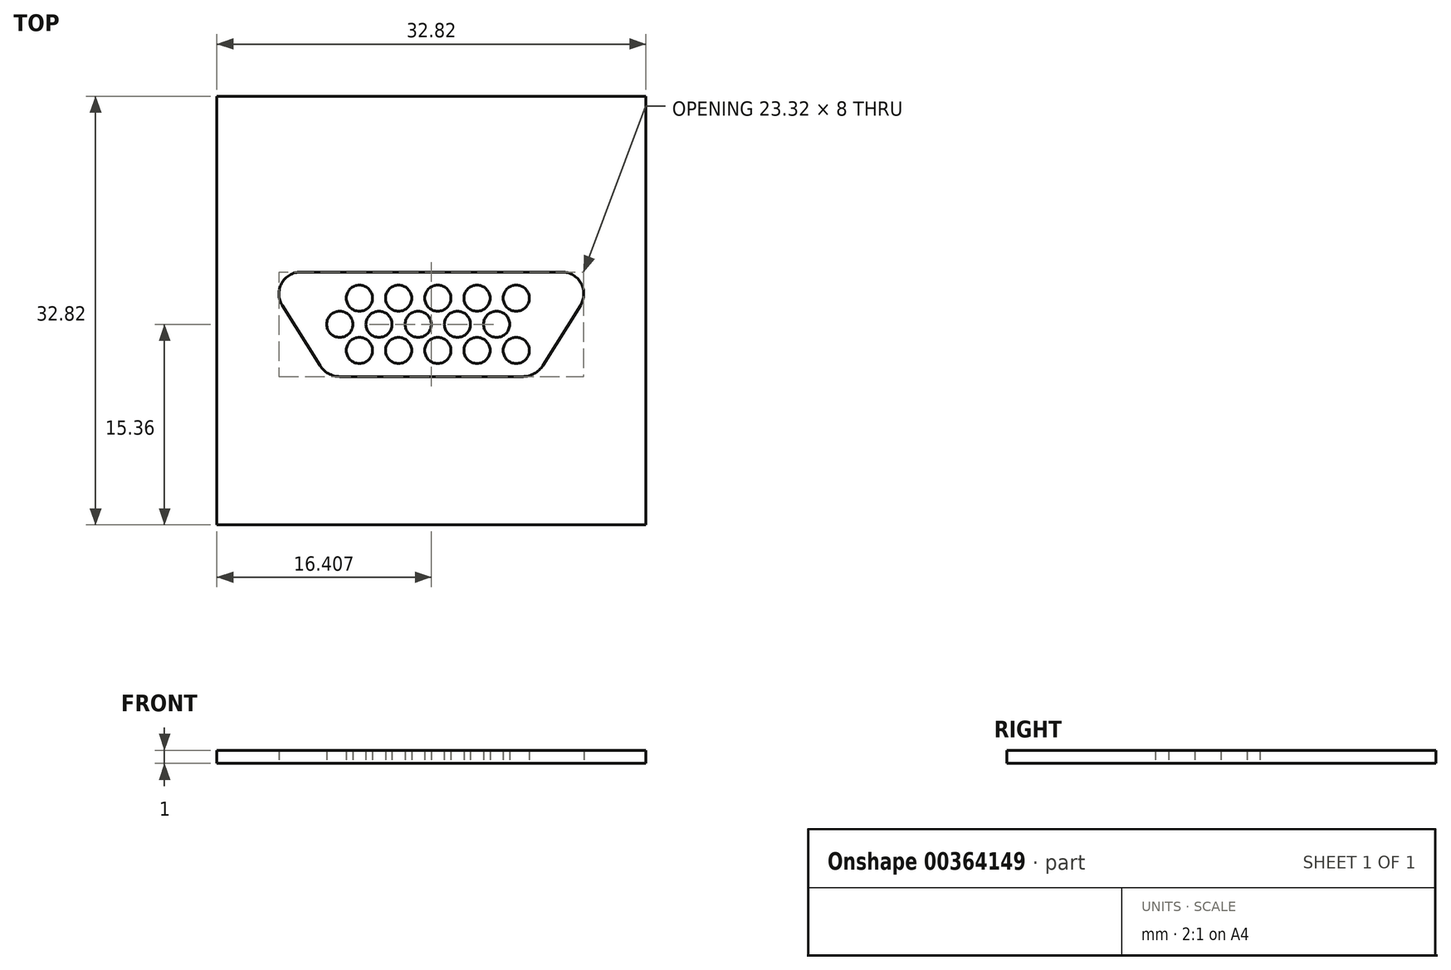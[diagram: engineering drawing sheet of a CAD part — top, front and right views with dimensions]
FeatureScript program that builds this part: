
annotation { "Feature Type Name" : "Feature", "Feature Type Description" : "" }
export const myFeature = defineFeature(function(context is Context, id is Id, definition is map)
    precondition{}
    {
        {
            var Q0;
            Q0=qCreatedBy(makeId("Top.planeOp"),FACE);
            var sketch = newSketch(context, id + "F0", { "sketchPlane" : qUnion([Q0])});
            skCircle(sketch, "E0", {"center": v(0, 0) * mm, "radius": 1 * mm});
            skCircle(sketch, "E1.1.0.0", {"center": v(3, 0) * mm, "radius": 1 * mm});
            skCircle(sketch, "E1.2.0.0", {"center": v(6, 0) * mm, "radius": 1 * mm});
            skLineSegment(sketch, "E1.direction1", {"start": v(0, 0) * mm, "end": v(3, 0) * mm, "construction": true});
            skCircle(sketch, "E2.1.0.0", {"center": v(-3, 0) * mm, "radius": 1 * mm});
            skCircle(sketch, "E2.2.0.0", {"center": v(-6, 0) * mm, "radius": 1 * mm});
            skLineSegment(sketch, "E2.direction1", {"start": v(0, 0) * mm, "end": v(-3, 0) * mm, "construction": true});
            skCircle(sketch, "E3", {"center": v(-4.5, 2) * mm, "radius": 1 * mm});
            skCircle(sketch, "E4.1.0.0", {"center": v(-1.5, 2) * mm, "radius": 1 * mm});
            skCircle(sketch, "E4.2.0.0", {"center": v(1.5, 2) * mm, "radius": 1 * mm});
            skCircle(sketch, "E4.3.0.0", {"center": v(4.5, 2) * mm, "radius": 1 * mm});
            skCircle(sketch, "E4.4.0.0", {"center": v(7.5, 2) * mm, "radius": 1 * mm});
            skLineSegment(sketch, "E4.direction1", {"start": v(-4.5, 2) * mm, "end": v(-1.5, 2) * mm, "construction": true});
            skCircle(sketch, "E5", {"center": v(-4.5, -2) * mm, "radius": 1 * mm});
            skCircle(sketch, "E6.1.0.0", {"center": v(-1.5, -2) * mm, "radius": 1 * mm});
            skCircle(sketch, "E6.2.0.0", {"center": v(1.5, -2) * mm, "radius": 1 * mm});
            skCircle(sketch, "E6.3.0.0", {"center": v(4.5, -2) * mm, "radius": 1 * mm});
            skCircle(sketch, "E6.4.0.0", {"center": v(7.5, -2) * mm, "radius": 1 * mm});
            skLineSegment(sketch, "E6.direction1", {"start": v(-4.5, -2) * mm, "end": v(-1.5, -2) * mm, "construction": true});
            skLineSegment(sketch, "E7", {"start": v(0, 4) * mm, "end": v(-9, 4) * mm});
            skLineSegment(sketch, "E8.MirrorCS", {"start": v(0, 4) * mm, "end": v(11, 4) * mm});
            skLineSegment(sketch, "E9", {"start": v(-10.4, 1.46) * mm, "end": v(-7.52, -3.15) * mm});
            skLineSegment(sketch, "E10", {"start": v(12.42, 1.46) * mm, "end": v(9.54, -3.15) * mm});
            skArc(sketch, "E11", {"start": v(-9, 4) * mm, "mid": v(-10.45, 3.14) * mm, "end": v(-10.4, 1.46) * mm});
            skArc(sketch, "E12", {"start": v(12.42, 1.46) * mm, "mid": v(12.46, 3.14) * mm, "end": v(11, 4) * mm});
            skLineSegment(sketch, "E13", {"start": v(-6, -4) * mm, "end": v(8, -4) * mm});
            skArc(sketch, "E14", {"start": v(-7.52, -3.15) * mm, "mid": v(-6.87, -3.77) * mm, "end": v(-6, -4) * mm});
            skArc(sketch, "E15", {"start": v(8, -4) * mm, "mid": v(8.88, -3.77) * mm, "end": v(9.54, -3.15) * mm});
            skLineSegment(sketch, "E16", {"start": v(17.42, 1.46) * mm, "end": v(17.42, 17.46) * mm});
            skLineSegment(sketch, "E17", {"start": v(17.42, 17.46) * mm, "end": v(-15.4, 17.46) * mm});
            skLineSegment(sketch, "E18.bottom", {"start": v(-15.4, 17.46) * mm, "end": v(17.42, 17.46) * mm});
            skLineSegment(sketch, "E18.top", {"start": v(-15.4, -15.36) * mm, "end": v(17.42, -15.36) * mm});
            skLineSegment(sketch, "E18.left", {"start": v(-15.4, 17.46) * mm, "end": v(-15.4, -15.36) * mm});
            skLineSegment(sketch, "E18.right", {"start": v(17.42, 17.46) * mm, "end": v(17.42, -15.36) * mm});
            skSolve(sketch);
        }
        {
            var Q0;
            Q0=makeQuery(id+"F0.imprint","IMPRINT",FACE,{"disambiguationData":[TD([[makeQuery(id+"F0.imprint","IMPRINT",EDGE,{"derivedFrom":sQuery(id+"F0.wireOp",EDGE,"E3")}),1.0]])]});
            var Q1;
            Q1=makeQuery(id+"F0.imprint","IMPRINT",FACE,{"disambiguationData":[TD([[makeQuery(id+"F0.imprint","IMPRINT",EDGE,{"derivedFrom":sQuery(id+"F0.wireOp",EDGE,"E4.1.0.0")}),1.0]])]});
            var Q2;
            Q2=makeQuery(id+"F0.imprint","IMPRINT",FACE,{"disambiguationData":[TD([[makeQuery(id+"F0.imprint","IMPRINT",EDGE,{"derivedFrom":sQuery(id+"F0.wireOp",EDGE,"E4.2.0.0")}),1.0]])]});
            var Q3;
            Q3=makeQuery(id+"F0.imprint","IMPRINT",FACE,{"disambiguationData":[TD([[makeQuery(id+"F0.imprint","IMPRINT",EDGE,{"derivedFrom":sQuery(id+"F0.wireOp",EDGE,"E4.3.0.0")}),1.0]])]});
            var Q4;
            Q4=makeQuery(id+"F0.imprint","IMPRINT",FACE,{"disambiguationData":[TD([[makeQuery(id+"F0.imprint","IMPRINT",EDGE,{"derivedFrom":sQuery(id+"F0.wireOp",EDGE,"E4.4.0.0")}),1.0]])]});
            var Q5;
            Q5=makeQuery(id+"F0.imprint","IMPRINT",FACE,{"disambiguationData":[TD([[makeQuery(id+"F0.imprint","IMPRINT",EDGE,{"derivedFrom":sQuery(id+"F0.wireOp",EDGE,"E1.2.0.0")}),1.0]])]});
            var Q6;
            Q6=makeQuery(id+"F0.imprint","IMPRINT",FACE,{"disambiguationData":[TD([[makeQuery(id+"F0.imprint","IMPRINT",EDGE,{"derivedFrom":sQuery(id+"F0.wireOp",EDGE,"E1.1.0.0")}),1.0]])]});
            var Q7;
            Q7=makeQuery(id+"F0.imprint","IMPRINT",FACE,{"disambiguationData":[TD([[makeQuery(id+"F0.imprint","IMPRINT",EDGE,{"derivedFrom":sQuery(id+"F0.wireOp",EDGE,"E0")}),1.0]])]});
            var Q8;
            Q8=makeQuery(id+"F0.imprint","IMPRINT",FACE,{"disambiguationData":[TD([[makeQuery(id+"F0.imprint","IMPRINT",EDGE,{"derivedFrom":sQuery(id+"F0.wireOp",EDGE,"E2.1.0.0")}),1.0]])]});
            var Q9;
            Q9=makeQuery(id+"F0.imprint","IMPRINT",FACE,{"disambiguationData":[TD([[makeQuery(id+"F0.imprint","IMPRINT",EDGE,{"derivedFrom":sQuery(id+"F0.wireOp",EDGE,"E2.2.0.0")}),1.0]])]});
            var Q10;
            Q10=makeQuery(id+"F0.imprint","IMPRINT",FACE,{"disambiguationData":[TD([[makeQuery(id+"F0.imprint","IMPRINT",EDGE,{"derivedFrom":sQuery(id+"F0.wireOp",EDGE,"E5")}),1.0]])]});
            var Q11;
            Q11=makeQuery(id+"F0.imprint","IMPRINT",FACE,{"disambiguationData":[TD([[makeQuery(id+"F0.imprint","IMPRINT",EDGE,{"derivedFrom":sQuery(id+"F0.wireOp",EDGE,"E6.1.0.0")}),1.0]])]});
            var Q12;
            Q12=makeQuery(id+"F0.imprint","IMPRINT",FACE,{"disambiguationData":[TD([[makeQuery(id+"F0.imprint","IMPRINT",EDGE,{"derivedFrom":sQuery(id+"F0.wireOp",EDGE,"E6.2.0.0")}),1.0]])]});
            var Q13;
            Q13=makeQuery(id+"F0.imprint","IMPRINT",FACE,{"disambiguationData":[TD([[makeQuery(id+"F0.imprint","IMPRINT",EDGE,{"derivedFrom":sQuery(id+"F0.wireOp",EDGE,"E6.3.0.0")}),1.0]])]});
            var Q14;
            Q14=makeQuery(id+"F0.imprint","IMPRINT",FACE,{"disambiguationData":[TD([[makeQuery(id+"F0.imprint","IMPRINT",EDGE,{"derivedFrom":sQuery(id+"F0.wireOp",EDGE,"E6.4.0.0")}),1.0]])]});
            extrude(context, id + "F1", {"entities" : qUnion([Q0, Q1, Q2, Q3, Q4, Q5, Q6, Q7, Q8, Q9, Q10, Q11, Q12, Q13, Q14]), "depth" : 1 * mm});
        }
        {
            var Q0;
            Q0=makeQuery(id+"F0.imprint","IMPRINT",FACE,{"disambiguationData":[TD([[makeQuery(id+"F0.imprint","IMPRINT",EDGE,{"derivedFrom":sQuery(id+"F0.wireOp",EDGE,"E7")}),-1.0]])]});
            extrude(context, id + "F2", {"entities" : qUnion([Q0]), "depth" : 1 * mm});
        }
    });
